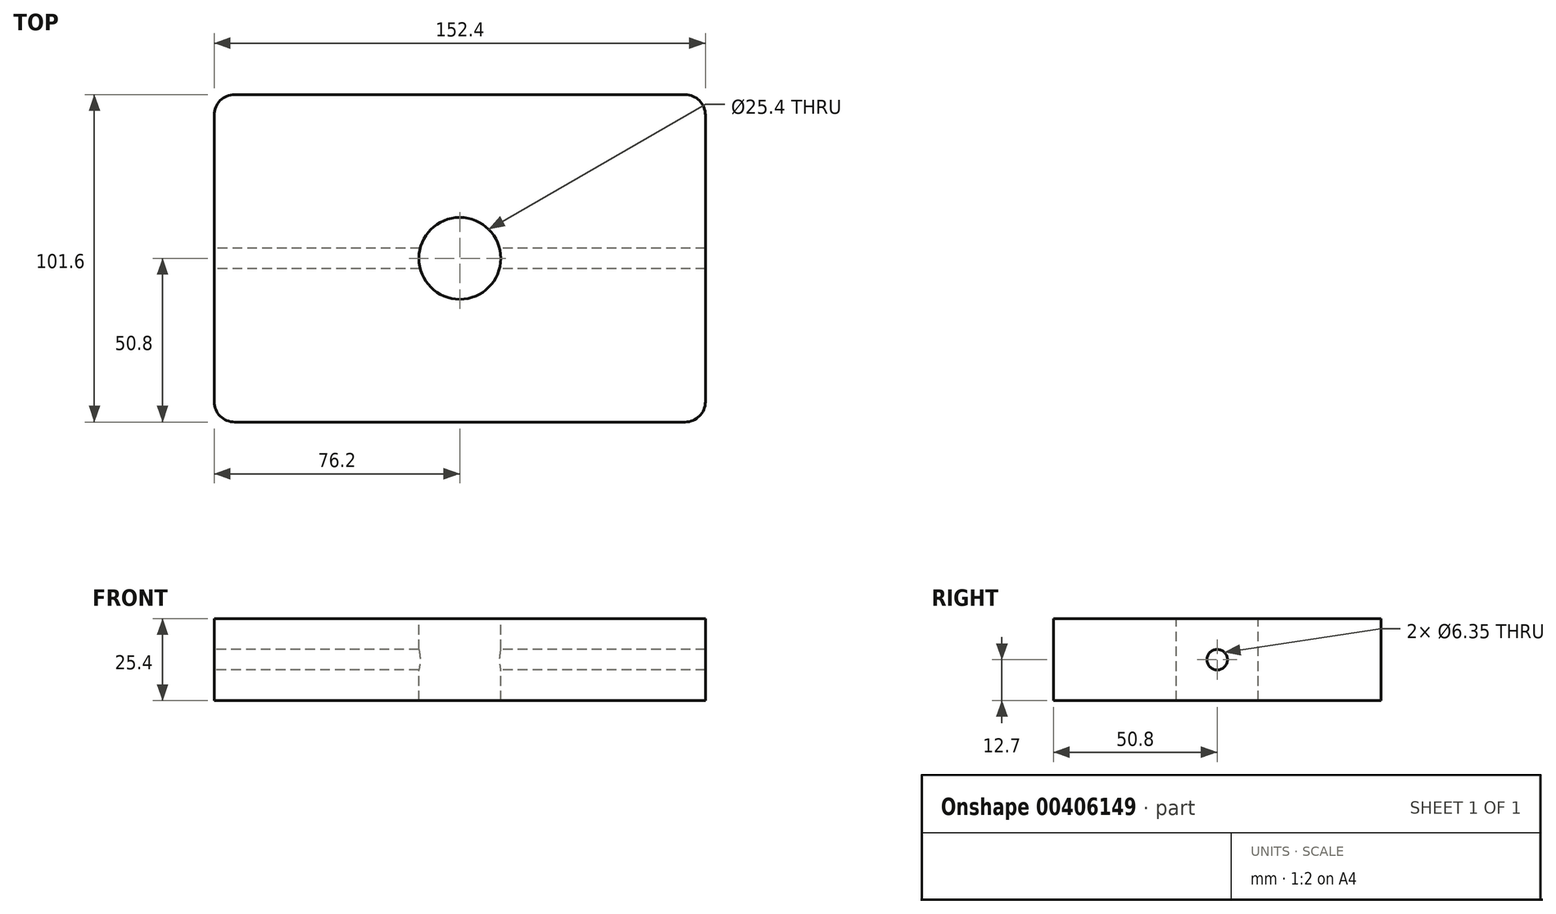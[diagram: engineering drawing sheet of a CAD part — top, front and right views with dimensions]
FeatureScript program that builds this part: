
annotation { "Feature Type Name" : "Feature", "Feature Type Description" : "" }
export const myFeature = defineFeature(function(context is Context, id is Id, definition is map)
    precondition{}
    {
        {
            var Q0;
            Q0=qCreatedBy(makeId("Top.planeOp"),FACE);
            var sketch = newSketch(context, id + "F0", { "sketchPlane" : qUnion([Q0])});
            skLineSegment(sketch, "E0.bottom", {"start": v(-69.85, 50.8) * mm, "end": v(69.85, 50.8) * mm});
            skLineSegment(sketch, "E0.top", {"start": v(-69.85, -50.8) * mm, "end": v(69.85, -50.8) * mm});
            skLineSegment(sketch, "E0.left", {"start": v(-76.2, 44.45) * mm, "end": v(-76.2, -44.45) * mm});
            skLineSegment(sketch, "E0.right", {"start": v(76.2, 44.45) * mm, "end": v(76.2, -44.45) * mm});
            skPoint(sketch, "E0.middle", {"position": v(0, 0) * mm});
            skPoint(sketch, "E1.visualSharp", {"position": v(-76.2, 50.8) * mm});
            skArc(sketch, "E1.filletArc", {"start": v(-69.85, 50.8) * mm, "mid": v(-74.34, 48.94) * mm, "end": v(-76.2, 44.45) * mm});
            skPoint(sketch, "E2.visualSharp", {"position": v(-76.2, -50.8) * mm});
            skArc(sketch, "E2.filletArc", {"start": v(-76.2, -44.45) * mm, "mid": v(-74.34, -48.94) * mm, "end": v(-69.85, -50.8) * mm});
            skPoint(sketch, "E3.visualSharp", {"position": v(76.2, -50.8) * mm});
            skArc(sketch, "E3.filletArc", {"start": v(69.85, -50.8) * mm, "mid": v(74.34, -48.94) * mm, "end": v(76.2, -44.45) * mm});
            skPoint(sketch, "E4.visualSharp", {"position": v(76.2, 50.8) * mm});
            skArc(sketch, "E4.filletArc", {"start": v(76.2, 44.45) * mm, "mid": v(74.34, 48.94) * mm, "end": v(69.85, 50.8) * mm});
            skSolve(sketch);
        }
        {
            var Q0;
            Q0 = qSketchRegion(id + "F0", true);
            extrude(context, id + "F1", {"entities" : qUnion([Q0]), "depth" : 25.4 * mm, "offsetDistance" : 25.4 * mm});
        }
        {
            var Q0;
            Q0=makeQuery(id+"F1.opExtrude","CAP_FACE",FACE,{"disambiguationData":[OSD([sQuery(id+"F0.wireOp",EDGE,"E0.bottom"),sQuery(id+"F0.wireOp",EDGE,"E0.top"),sQuery(id+"F0.wireOp",EDGE,"E0.left"),sQuery(id+"F0.wireOp",EDGE,"E0.right"),sQuery(id+"F0.wireOp",EDGE,"E1.filletArc"),sQuery(id+"F0.wireOp",EDGE,"E2.filletArc"),sQuery(id+"F0.wireOp",EDGE,"E3.filletArc"),sQuery(id+"F0.wireOp",EDGE,"E4.filletArc")])],"isStart":false});
            var sketch = newSketch(context, id + "F2", { "sketchPlane" : qUnion([Q0])});
            skCircle(sketch, "E5", {"center": v(0, 0) * mm, "radius": 12.7 * mm});
            skSolve(sketch);
        }
        {
            var Q0;
            Q0 = qSketchRegion(id + "F2", true);
            extrude(context, id + "F3", {"entities" : qUnion([Q0]), "operationType" : NewBodyOperationType.REMOVE, "endBound" : BoundingType.THROUGH_ALL, "oppositeDirection" : true, "depth" : 25.4 * mm, "offsetDistance" : 25.4 * mm});
        }
        {
            var Q0;
            Q0=makeQuery(id+"F1.opExtrude","SWEPT_FACE",FACE,{"disambiguationData":[OSD([sQuery(id+"F0.wireOp",EDGE,"E0.left")])]});
            var sketch = newSketch(context, id + "F4", { "sketchPlane" : qUnion([Q0])});
            skLineSegment(sketch, "E6.0", {"start": v(-12.7, 0) * mm, "end": v(12.7, 0) * mm});
            skLineSegment(sketch, "E7.0.0", {"start": v(44.45, 0) * mm, "end": v(-44.45, 0) * mm});
            skLineSegment(sketch, "E7.0.1", {"start": v(-44.45, 0) * mm, "end": v(-50.8, 0) * mm});
            skLineSegment(sketch, "E7.0.3", {"start": v(-50.8, 0) * mm, "end": v(-44.45, 0) * mm});
            skLineSegment(sketch, "E7.0.4", {"start": v(-44.45, 0) * mm, "end": v(44.45, 0) * mm});
            skLineSegment(sketch, "E7.0.5", {"start": v(44.45, 0) * mm, "end": v(50.8, 0) * mm});
            skLineSegment(sketch, "E7.0.7", {"start": v(50.8, 0) * mm, "end": v(44.45, 0) * mm});
            skPoint(sketch, "E8.0", {"position": v(0, 0) * mm});
            skLineSegment(sketch, "E9", {"start": v(0, 0) * mm, "end": v(0, 25.4) * mm});
            skLineSegment(sketch, "E10", {"start": v(0, 12.7) * mm, "end": v(-24.56, 12.7) * mm});
            skCircle(sketch, "E11", {"center": v(0, 12.7) * mm, "radius": 3.18 * mm});
            skSolve(sketch);
        }
        {
            var Q0;
            Q0 = qSketchRegion(id + "F4", true);
            extrude(context, id + "F5", {"entities" : qUnion([Q0]), "operationType" : NewBodyOperationType.REMOVE, "endBound" : BoundingType.THROUGH_ALL, "oppositeDirection" : true, "depth" : 25.4 * mm, "offsetDistance" : 25.4 * mm});
        }
    });
